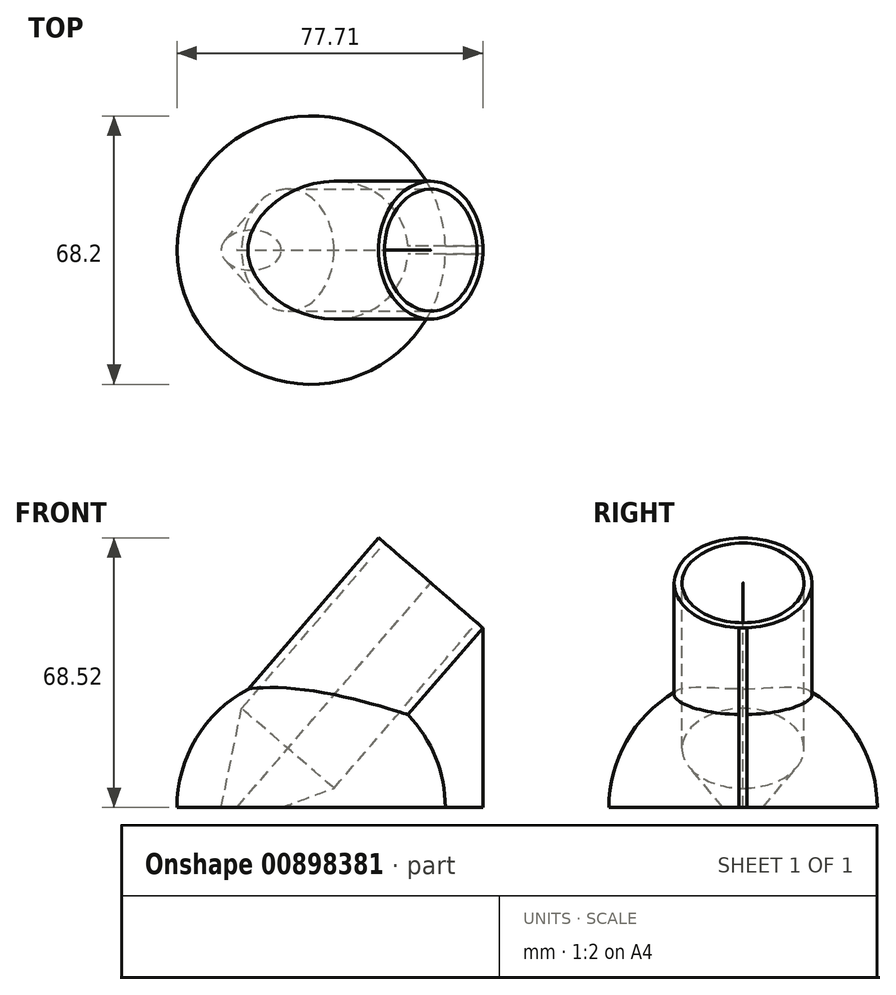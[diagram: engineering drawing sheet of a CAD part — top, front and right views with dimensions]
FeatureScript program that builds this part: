
annotation { "Feature Type Name" : "Feature", "Feature Type Description" : "" }
export const myFeature = defineFeature(function(context is Context, id is Id, definition is map)
    precondition{}
    {
        {
            var Q0;
            Q0=qCreatedBy(makeId("Front.planeOp"),FACE);
            var sketch = newSketch(context, id + "F0", { "sketchPlane" : qUnion([Q0])});
            skLineSegment(sketch, "E0", {"start": v(4.2, 0) * mm, "end": v(43.61, 45.65) * mm});
            skLineSegment(sketch, "E1", {"start": v(43.61, 45.65) * mm, "end": v(17.12, 68.52) * mm});
            skLineSegment(sketch, "E2", {"start": v(17.12, 68.52) * mm, "end": v(-22.29, 22.87) * mm});
            skLineSegment(sketch, "E3", {"start": v(-22.29, 22.87) * mm, "end": v(4.2, 0) * mm});
            skLineSegment(sketch, "E4", {"start": v(-9.04, 11.44) * mm, "end": v(30.37, 57.09) * mm});
            skSolve(sketch);
        }
        {
            var Q0;
            {var subQ0=sQuery(id+"F0.wireOp",EDGE,"E0");Q0=makeQuery(id+"F0.imprint","IMPRINT",FACE,{"disambiguationData":[TD([[makeQuery(id+"F0.imprint","IMPRINT",EDGE,{"derivedFrom":subQ0}),1.0]])]});}
            var Q1;
            Q1=sQuery(id+"F0.wireOp",EDGE,"E4");
            revolve(context, id + "F1", {"surfaceOperationType" : NewSurfaceOperationType.NEW, "entities" : qUnion([Q0]), "axis" : qUnion([Q1]), "revolveType" : RevolveType.FULL});
        }
        {
            var Q0;
            Q0=qCreatedBy(makeId("Front.planeOp"),FACE);
            var sketch = newSketch(context, id + "F2", { "sketchPlane" : qUnion([Q0])});
            skLineSegment(sketch, "E5", {"start": v(0, 34.1) * mm, "end": v(0, 0) * mm});
            skLineSegment(sketch, "E6", {"start": v(0, 0) * mm, "end": v(34.1, 0) * mm});
            skArc(sketch, "E7", {"start": v(34.1, 0) * mm, "mid": v(24.11, 24.11) * mm, "end": v(0, 34.1) * mm});
            skSolve(sketch);
        }
        {
            var Q0;
            Q0=makeQuery(id+"F2.imprint","IMPRINT",FACE,{"disambiguationData":[TD([[makeQuery(id+"F2.imprint","IMPRINT",EDGE,{"derivedFrom":sQuery(id+"F2.wireOp",EDGE,"E5")}),1.0]])]});
            var Q1;
            Q1=sQuery(id+"F2.wireOp",EDGE,"E5");
            revolve(context, id + "F3", {"operationType" : NewBodyOperationType.ADD, "surfaceOperationType" : NewSurfaceOperationType.NEW, "entities" : qUnion([Q0]), "axis" : qUnion([Q1]), "revolveType" : RevolveType.FULL});
        }
        {
            var Q0;
            Q0=qCreatedBy(makeId("Front.planeOp"),FACE);
            var sketch = newSketch(context, id + "F4", { "sketchPlane" : qUnion([Q0])});
            skLineSegment(sketch, "E8", {"start": v(0, 0) * mm, "end": v(43.61, 0) * mm});
            skLineSegment(sketch, "E9", {"start": v(43.61, 0) * mm, "end": v(43.61, 45.65) * mm});
            skLineSegment(sketch, "E10", {"start": v(43.61, 45.65) * mm, "end": v(30.17, 57.26) * mm});
            skLineSegment(sketch, "E11", {"start": v(30.17, 57.26) * mm, "end": v(0, 22.32) * mm});
            skLineSegment(sketch, "E12", {"start": v(0, 22.32) * mm, "end": v(0, 0) * mm});
            skLineSegment(sketch, "E13", {"start": v(43.61, 45.65) * mm, "end": v(29.27, 29.04) * mm});
            skLineSegment(sketch, "E14", {"start": v(-6.95, 40.64) * mm, "end": v(33, 86.9) * mm});
            skLineSegment(sketch, "E15", {"start": v(59.49, 64.04) * mm, "end": v(29.27, 29.04) * mm});
            skSolve(sketch);
        }
        {
            var Q0;
            Q0=makeQuery(id+"F4.imprint","IMPRINT",FACE,{"disambiguationData":[TD([[makeQuery(id+"F4.imprint","IMPRINT",EDGE,{"derivedFrom":sQuery(id+"F4.wireOp",EDGE,"E8")}),1.0]])]});
            extrude(context, id + "F5", {"entities" : qUnion([Q0]), "operationType" : NewBodyOperationType.ADD, "depth" : 2 * mm, "offsetDistance" : 25 * mm, "symmetric" : true});
        }
        {
            var Q0;
            Q0=qCreatedBy(makeId("Front.planeOp"),FACE);
            var sketch = newSketch(context, id + "F6", { "sketchPlane" : qUnion([Q0])});
            skLineSegment(sketch, "E16.0", {"start": v(43.6, 45.67) * mm, "end": v(17.12, 68.52) * mm});
            skLineSegment(sketch, "E17", {"start": v(18.64, 67.21) * mm, "end": v(-17.66, 25.17) * mm});
            skLineSegment(sketch, "E18", {"start": v(-17.66, 25.17) * mm, "end": v(-24.12, -6) * mm});
            skLineSegment(sketch, "E19", {"start": v(-24.12, -6) * mm, "end": v(5.78, 4.93) * mm});
            skLineSegment(sketch, "E20", {"start": v(5.78, 4.93) * mm, "end": v(42.08, 46.97) * mm});
            skLineSegment(sketch, "E21", {"start": v(42.08, 46.97) * mm, "end": v(18.64, 67.21) * mm});
            skLineSegment(sketch, "E22", {"start": v(-24.12, -6) * mm, "end": v(30.36, 57.1) * mm});
            skLineSegment(sketch, "E23", {"start": v(-6.95, 40.64) * mm, "end": v(33, 86.9) * mm});
            skLineSegment(sketch, "E24.0", {"start": v(43.6, 45.67) * mm, "end": v(24.56, 23.63) * mm});
            skSolve(sketch);
        }
        {
            var Q0;
            Q0=makeQuery(id+"F6.imprint","IMPRINT",FACE,{"disambiguationData":[TD([[makeQuery(id+"F6.imprint","IMPRINT",EDGE,{"derivedFrom":sQuery(id+"F6.wireOp",EDGE,"E17")}),1.0]])]});
            var Q1;
            Q1=sQuery(id+"F0.wireOp",EDGE,"E4");
            revolve(context, id + "F7", {"operationType" : NewBodyOperationType.REMOVE, "surfaceOperationType" : NewSurfaceOperationType.NEW, "entities" : qUnion([Q0]), "axis" : qUnion([Q1]), "revolveType" : RevolveType.FULL, "oppositeDirection" : true});
        }
    });
